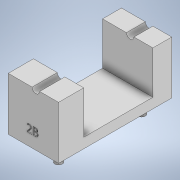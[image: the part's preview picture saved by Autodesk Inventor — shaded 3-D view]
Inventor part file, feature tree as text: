
AUTODESK INVENTOR PART (.ipt)
format: ipt  version: 2021 (Build 250183000, 183)  size: 217,600 bytes
history: native  units: mm
features: sketch x5, extrude x4, emboss x1
ambient origin geometry x8: Origin, YZ Plane, XZ Plane, XY Plane, X Axis, Y Axis, Z Axis, Center Point
bodies: Solid1 (feature_tree)
feature tree (10):
  extrude  "Extrusion1"  Depth=21.0mm
  extrude  "Extrusion2"  Depth=20.0mm TaperAngle=0.0deg
  extrude  "Extrusion3"  Depth=3.0mm
  extrude  "Extrusion4"  Depth=3.5mm
  emboss  "Emboss1"
  sketch  "Sketch1"  dims[d0=45.0mm d1=21.0mm]
  sketch  "Sketch2"  dims[d2=10.5mm d4=20.0mm d5=0.0mm]
  sketch  "Sketch3"  dims[d6=3.0mm d7=3.0mm]
  sketch  "Sketch4"  dims[d8=33.0mm d10=3.5mm]
  sketch  "Sketch5"  dims[d12=3.5mm d13=3.0mm d14=0.0mm d15=17.5mm d17=7.5mm d18=4.0mm d19=0.0mm d20=0.0mm d21=3.0mm d23=0.0mm d24=0.0mm d25=10.0mm d26=1.0mm d27=0.0mm d28=11.0mm]
